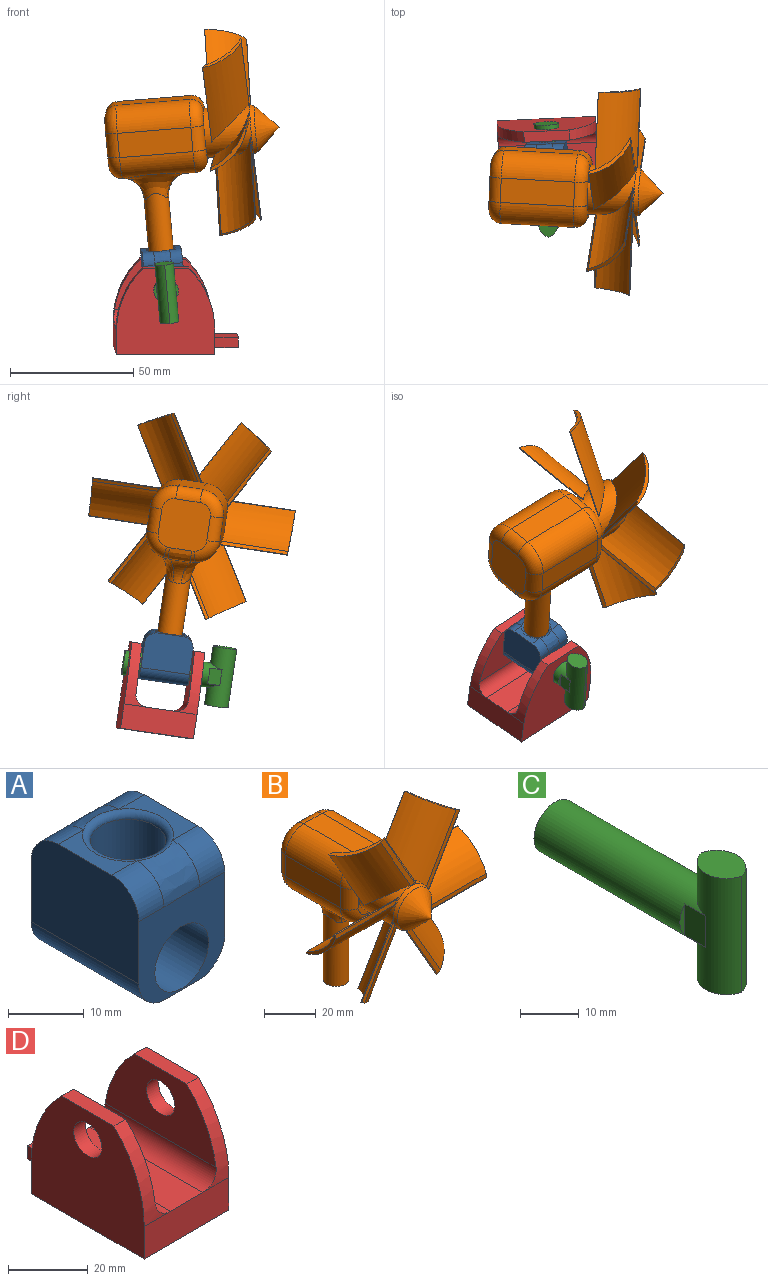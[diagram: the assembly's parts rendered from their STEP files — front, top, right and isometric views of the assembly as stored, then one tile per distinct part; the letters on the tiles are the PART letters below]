
ASSEMBLY  parts=4 mates=3
PART A: 19 faces, bbox 16x20x20 mm
  f0: plane 10x4.68mm, normal (0,0,1), area 28mm2, adj f2,f10,f13,f16
  f1: plane 20x6mm, normal (0,0,-1), area 120mm2, adj f6,f7,f11,f12
  f2: plane 20x15mm, normal (1,0,0), area 289.3mm2, adj f0,f6,f7,f11,f13,f16
  f3: plane 10x4.68mm, normal (0,0,1), area 28mm2, adj f4,f10,f15,f18
  f4: plane 20x15mm, normal (-1,0,0), area 289.3mm2, adj f3,f6,f7,f12,f15,f18
  f5: cylinder r=5mm len=20mm, axis (0,1,0), area 628.3mm2, adj f6,f7
  f6: plane 16x15.1mm, normal (0,-1,0), area 151.1mm2, adj f1,f2,f4,f5,f11,f12,f16,f17
  f7: plane 16x15.1mm, normal (0,1,0), area 151.1mm2, adj f1,f2,f4,f5,f11,f12,f13,f14
  f8: cylinder r=5mm len=10mm, axis (0,0,1), area 251.3mm2, adj f9,f10
  f9: plane 10x10mm, normal (0,0,1), area 78.5mm2, adj f8
  f10: torus R=6mm, axis (0,0,1), area 52.9mm2, adj f0,f3,f8,f14,f17
  f11: cylinder r=5mm len=20mm, axis (0,-1,0), area 157.1mm2, adj f1,f2,f6,f7
  f12: cylinder r=5mm len=20mm, axis (0,1,0), area 157.1mm2, adj f1,f4,f6,f7
  f13: cylinder r=5mm len=5mm, axis (-1,0,0), area 36.8mm2, adj f0,f2,f7,f14
  f14: bspline ~6.63x5mm, area 47.6mm2, adj f7,f10,f13,f15
  f15: cylinder r=5mm len=5mm, axis (-1,0,0), area 36.8mm2, adj f3,f4,f7,f14
  f16: cylinder r=5mm len=5mm, axis (1,0,0), area 36.8mm2, adj f0,f2,f6,f17
  f17: bspline ~6.63x5mm, area 47.6mm2, adj f6,f10,f16,f18
  f18: cylinder r=5mm len=5mm, axis (1,0,0), area 36.8mm2, adj f3,f4,f6,f17
PART B: 82 faces, bbox 82.9x70x95.7 mm
  f0: plane 10x10mm, normal (0,-1,0), area 16.1mm2, adj f4,f75,f77,f79
  f1: plane 10x10mm, normal (0,-1,0), area 16.1mm2, adj f4,f79,f80,f81
  f2: plane 10x10mm, normal (0,-1,0), area 16.1mm2, adj f4,f76,f78,f80
  f3: plane 10x3.18mm, normal (0,0,-1), area 26mm2, adj f11,f12,f62,f79
  f4: cylinder r=10mm len=20mm, axis (0,1,0), area 955.4mm2, adj f0,f1,f2,f8,f15,f16,f17,f18
  f5: plane 30x10mm, normal (0,0,1), area 300mm2, adj f10,f13,f67,f76
  f6: plane 30x10mm, normal (-1,0,0), area 300mm2, adj f10,f11,f64,f75
  f7: plane 30x10mm, normal (1,0,0), area 300mm2, adj f12,f13,f71,f80
  f8: plane 10x10mm, normal (0,-1,0), area 16.1mm2, adj f4,f74,f75,f76
  f9: plane 20.18x20mm, normal (0,1,0), area 379.9mm2, adj f64,f65,f66,f67,f68,f69,f70,f71
  f10: cylinder r=10mm len=30mm, axis (0,-1,0), area 471.2mm2, adj f5,f6,f65,f74
  f11: cylinder r=10mm len=30mm, axis (0,1,0), area 365.9mm2, adj f3,f6,f60,f66,f77
  f12: cylinder r=10mm len=30mm, axis (0,-1,0), area 365.9mm2, adj f3,f7,f63,f73,f81
  f13: cylinder r=10mm len=30mm, axis (0,1,0), area 471.2mm2, adj f5,f7,f69,f78
  f14: cone r=10mm half-angle=45deg, axis (0,1,0), area 383.7mm2, adj f15
  f15: cone r=10mm half-angle=22.5deg, axis (0,1,0), area 112mm2, adj f4,f14
  f16: cylinder r=23.44mm len=38.77mm, axis (-1,0,0), area 804.1mm2, adj f4,f19,f20,f21
  f17: cylinder r=26.89mm len=35.59mm, axis (-1,0,0), area 781.8mm2, adj f4,f18,f20,f22
  f18: plane 34.77x0.38mm, normal (0,-0.94,-0.35), area 14.1mm2, adj f4,f17,f20,f21
  f19: plane 38.77x0.21mm, normal (0,0.99,0.14), area 8.2mm2, adj f4,f16,f20,f22
  f20: plane 17.07x15.91mm, normal (1,0,0), area 32mm2, adj f16,f17,f18,f19,f21,f22
  f21: plane 34.36x2.02mm, normal (0,-1,-0.01), area 67.8mm2, adj f4,f16,f18,f20
  f22: plane 38.1x1.32mm, normal (0,0.87,-0.5), area 55.8mm2, adj f4,f17,f19,f20
  f23: cylinder r=23.44mm len=40.91mm, axis (-0.5,0,0.87), area 751.6mm2, adj f4,f26,f27,f28
  f24: cylinder r=26.89mm len=38.59mm, axis (-0.5,0,0.87), area 727.8mm2, adj f4,f25,f27,f29
  f25: plane 30.11x17.71mm, normal (-0.3,-0.94,-0.18), area 14.1mm2, adj f4,f24,f27,f28
  f26: plane 33.68x19.39mm, normal (0.12,0.99,0.07), area 8.2mm2, adj f4,f23,f27,f29
  f27: plane 15.91x14.79mm, normal (0.5,0,-0.87), area 32mm2, adj f23,f24,f25,f26,f28,f29
  f28: plane 29.76x18.93mm, normal (-0.01,-1,0), area 67.8mm2, adj f4,f23,f25,f27
  f29: plane 33.66x19.05mm, normal (-0.43,0.87,-0.25), area 55.8mm2, adj f4,f24,f26,f27
  f30: cylinder r=23.44mm len=40.91mm, axis (0.5,0,0.87), area 766.9mm2, adj f4,f33,f34,f35
  f31: cylinder r=26.89mm len=38.59mm, axis (0.5,0,0.87), area 753.3mm2, adj f4,f32,f34,f36
  f32: plane 30.3x17.51mm, normal (-0.3,-0.94,0.18), area 14.1mm2, adj f4,f31,f34,f35
  f33: plane 33.58x19.57mm, normal (0.12,0.99,-0.07), area 8.2mm2, adj f4,f30,f34,f36
  f34: plane 15.91x14.79mm, normal (-0.5,0,-0.87), area 32mm2, adj f30,f31,f32,f33,f35,f36
  f35: plane 30.77x18.16mm, normal (-0.01,-1,0), area 67.8mm2, adj f4,f30,f32,f34
  f36: plane 33x20.19mm, normal (-0.43,0.87,0.25), area 55.8mm2, adj f4,f31,f33,f34
  f37: cylinder r=23.44mm len=38.77mm, axis (1,0,0), area 804.1mm2, adj f4,f40,f41,f42
  f38: cylinder r=26.89mm len=35.59mm, axis (1,0,0), area 781.8mm2, adj f4,f39,f41,f43
  f39: plane 34.77x0.38mm, normal (0,-0.94,0.35), area 14.1mm2, adj f4,f38,f41,f42
  f40: plane 38.77x0.21mm, normal (0,0.99,-0.14), area 8.2mm2, adj f4,f37,f41,f43
  f41: plane 17.07x15.91mm, normal (-1,0,0), area 32mm2, adj f37,f38,f39,f40,f42,f43
  f42: plane 34.36x2.02mm, normal (0,-1,0.01), area 67.8mm2, adj f4,f37,f39,f41
  f43: plane 38.1x1.32mm, normal (0,0.87,0.5), area 55.8mm2, adj f4,f38,f40,f41
  f44: cylinder r=23.44mm len=40.91mm, axis (0.5,0,-0.87), area 804.1mm2, adj f4,f47,f48,f49
  f45: cylinder r=26.89mm len=38.59mm, axis (0.5,0,-0.87), area 781.8mm2, adj f4,f46,f48,f50
  f46: plane 30.11x17.71mm, normal (0.3,-0.94,0.18), area 14.1mm2, adj f4,f45,f48,f49
  f47: plane 33.68x19.39mm, normal (-0.12,0.99,-0.07), area 8.2mm2, adj f4,f44,f48,f50
  f48: plane 15.91x14.79mm, normal (-0.5,0,0.87), area 32mm2, adj f44,f45,f46,f47,f49,f50
  f49: plane 29.76x18.93mm, normal (0.01,-1,0), area 67.8mm2, adj f4,f44,f46,f48
  f50: plane 33.66x19.05mm, normal (0.43,0.87,0.25), area 55.8mm2, adj f4,f45,f47,f48
  f51: cylinder r=23.44mm len=40.91mm, axis (-0.5,0,-0.87), area 804.1mm2, adj f4,f54,f55,f56
  f52: cylinder r=26.89mm len=38.59mm, axis (-0.5,0,-0.87), area 781.8mm2, adj f4,f53,f55,f57
  f53: plane 30.3x17.51mm, normal (0.3,-0.94,-0.18), area 14.1mm2, adj f4,f52,f55,f56
  f54: plane 33.58x19.57mm, normal (-0.12,0.99,0.07), area 8.2mm2, adj f4,f51,f55,f57
  f55: plane 15.91x14.79mm, normal (0.5,0,0.87), area 32mm2, adj f51,f52,f53,f54,f56,f57
  f56: plane 30.77x18.16mm, normal (0.01,-1,0), area 67.8mm2, adj f4,f51,f53,f55
  f57: plane 33x20.19mm, normal (0.43,0.87,-0.25), area 55.8mm2, adj f4,f52,f54,f55
  f58: cylinder r=5mm len=32.68mm, axis (0,0,1), area 975.7mm2, adj f59,f60,f61,f62,f63
  f59: plane 10x10mm, normal (0,0,-1), area 78.5mm2, adj f58
  f60: bspline ~29.68x11.35mm, area 232.8mm2, adj f11,f58,f61,f62,f68
  f61: torus R=15mm, axis (0,0,1), area 78.7mm2, adj f58,f60,f63,f70
  f62: torus R=15mm, axis (0,0,1), area 92.2mm2, adj f3,f58,f60,f63
  f63: bspline ~29.68x11.35mm, area 232.8mm2, adj f12,f58,f61,f62,f72
  f64: cylinder r=5mm len=10mm, axis (0,0,-1), area 78.5mm2, adj f6,f9,f65,f66
  f65: torus R=5mm, axis (0,-1,0), area 101mm2, adj f9,f10,f64,f67
  f66: torus R=5mm, axis (0,-1,0), area 91.2mm2, adj f9,f11,f64,f68
  f67: cylinder r=5mm len=10mm, axis (-1,0,0), area 78.5mm2, adj f5,f9,f65,f69
  f68: bspline ~5.39x5.33mm, area 12.5mm2, adj f9,f60,f66,f70
  f69: torus R=5mm, axis (0,-1,0), area 101mm2, adj f9,f13,f67,f71
  f70: bspline ~11.33x5.08mm, area 65.9mm2, adj f9,f61,f68,f72
  f71: cylinder r=5mm len=10mm, axis (0,0,1), area 78.5mm2, adj f7,f9,f69,f73
  f72: bspline ~5.16x5.11mm, area 12.5mm2, adj f9,f63,f70,f73
  f73: torus R=5mm, axis (0,-1,0), area 91.2mm2, adj f9,f12,f71,f72
  f74: torus R=5mm, axis (0,-1,0), area 101mm2, adj f8,f10,f75,f76
  f75: cylinder r=5mm len=10mm, axis (0,0,1), area 78.5mm2, adj f0,f6,f8,f74,f77
  f76: cylinder r=5mm len=10mm, axis (1,0,0), area 78.5mm2, adj f2,f5,f8,f74,f78
  f77: torus R=5mm, axis (0,-1,0), area 101mm2, adj f0,f11,f75,f79
  f78: torus R=5mm, axis (0,-1,0), area 101mm2, adj f2,f13,f76,f80
  f79: cylinder r=5mm len=10mm, axis (-1,0,0), area 78.5mm2, adj f0,f1,f3,f77,f81
  f80: cylinder r=5mm len=10mm, axis (0,0,-1), area 78.5mm2, adj f1,f2,f7,f78,f81
  f81: torus R=5mm, axis (0,-1,0), area 101mm2, adj f1,f12,f79,f80
PART C: 10 faces, bbox 10x44.9x24.1 mm
  f0: plane 6.49x1.2mm, normal (0,-1,0), area 5.3mm2, adj f1,f4
  f1: cylinder r=5mm len=40mm, axis (0,1,0), area 1126.1mm2, adj f0,f2,f3,f4,f6,f8,f9
  f2: plane 6.49x1.2mm, normal (0,-1,0), area 5.3mm2, adj f1,f6
  f3: plane 10x10mm, normal (0,1,0), area 78.5mm2, adj f1
  f4: plane 6.49x5mm, normal (-1,0,0), area 32.5mm2, adj f0,f1,f8
  f5: plane 9.71x7.6mm, normal (0,0,-1), area 54.8mm2, adj f8,f9
  f6: plane 6.49x5mm, normal (1,0,0), area 32.5mm2, adj f1,f2,f9
  f7: plane 9.71x7.6mm, normal (0,0,1), area 54.8mm2, adj f8,f9
  f8: cylinder r=5mm len=24.12mm, axis (0,0,-1), area 265.4mm2, adj f1,f4,f5,f7,f9
  f9: cylinder r=5mm len=24.12mm, axis (0,0,1), area 265.4mm2, adj f1,f5,f6,f7,f8
PART D: 28 faces, bbox 30x50x35.4 mm
  f0: plane 18.49x4.21mm, normal (0,0,1), area 77.8mm2, adj f1,f2,f3,f13
  f1: cylinder r=35.35mm len=25.39mm, axis (-1,0,0), area 124.6mm2, adj f0,f3,f7,f13,f17
  f2: cylinder r=35.35mm len=25.39mm, axis (-1,0,0), area 124.6mm2, adj f0,f3,f6,f13,f17
  f3: plane 40x35.39mm, normal (-1,0,0), area 1167.8mm2, adj f0,f1,f2,f4,f6,f7,f14
  f4: plane 40x30mm, normal (0,0,-1), area 1200mm2, adj f3,f5,f6,f7
  f5: plane 40x35.39mm, normal (1,0,0), area 1167.8mm2, adj f4,f6,f7,f8,f9,f10,f15
  f6: plane 30x10mm, normal (0,-1,0), area 300mm2, adj f2,f3,f4,f5,f10,f12
  f7: plane 30x10mm, normal (0,1,0), area 250mm2, adj f1,f3,f4,f5,f9,f12,f18,f19
  f8: plane 18.49x4.21mm, normal (0,0,1), area 77.8mm2, adj f5,f9,f10,f11
  f9: cylinder r=35.35mm len=25.39mm, axis (-1,0,0), area 124.6mm2, adj f5,f7,f8,f11,f16
  f10: cylinder r=35.35mm len=25.39mm, axis (-1,0,0), area 124.6mm2, adj f5,f6,f8,f11,f16
  f11: plane 39.29x20.39mm, normal (-1,0,0), area 569mm2, adj f8,f9,f10,f15,f16
  f12: plane 40x11.58mm, normal (0,0,1), area 463.3mm2, adj f6,f7,f16,f17
  f13: plane 39.29x20.39mm, normal (1,0,0), area 569mm2, adj f0,f1,f2,f14,f17
  f14: cylinder r=5mm len=10mm, axis (1,0,0), area 132.2mm2, adj f3,f13
  f15: cylinder r=5mm len=10mm, axis (1,0,0), area 132.2mm2, adj f5,f11
  f16: cylinder r=5mm len=40mm, axis (0,1,0), area 312.9mm2, adj f9,f10,f11,f12
  f17: cylinder r=5mm len=40mm, axis (0,-1,0), area 312.9mm2, adj f1,f2,f12,f13
  f18: plane 12.38x10mm, normal (0,0,1), area 123.8mm2, adj f7,f19,f25,f26
  f19: plane 10x4.04mm, normal (1,0,0), area 40.4mm2, adj f7,f18,f20,f26
  f20: plane 12.38x10mm, normal (0,0,-1), area 123.8mm2, adj f7,f19,f25,f26
  f21: plane 10x0.91mm, normal (-1,0,0), area 9.1mm2, adj f22,f24,f26,f27
  f22: plane 10.17x10mm, normal (0,0,-1), area 101.7mm2, adj f21,f23,f26,f27
  f23: plane 10x0.91mm, normal (1,0,0), area 9.1mm2, adj f22,f24,f26,f27
  f24: plane 10.17x10mm, normal (0,0,1), area 101.7mm2, adj f21,f23,f26,f27
  f25: plane 10x4.04mm, normal (-1,0,0), area 40.4mm2, adj f7,f18,f20,f26
  f26: plane 12.38x4.04mm, normal (0,1,0), area 40.8mm2, adj f18,f19,f20,f21,f22,f23,f24,f25
  f27: plane 10.17x0.91mm, normal (0,1,0), area 9.3mm2, adj f21,f22,f23,f24
PLACE A rot(axis=(0.83,-0.52,0.22),10.1deg) t=(2.7,48.5,38.35)mm
PLACE B rot(axis=(0.03,-0.12,0.99),87.7deg) t=(-19.37,28.62,84.67)mm
PLACE C rot(axis=(0.83,-0.52,0.22),10.1deg) t=(2.58,56.31,33.27)mm
PLACE D rot(axis=(0.07,0.07,-0.99),87.7deg) t=(23.07,48.14,5.14)mm
MATE fastened A.f5 <-> C.f1  axis (-0.05,0.99,0.14) through (2.9,49.39,32.27)mm
MATE revolute B.f58 <-> A.f8  axis (0.09,0.15,-0.99) through (2.85,38.66,36.5)mm
MATE revolute D.f14 <-> C.f1  axis (0.05,-0.99,-0.14) through (2.85,50.38,32.41)mm
